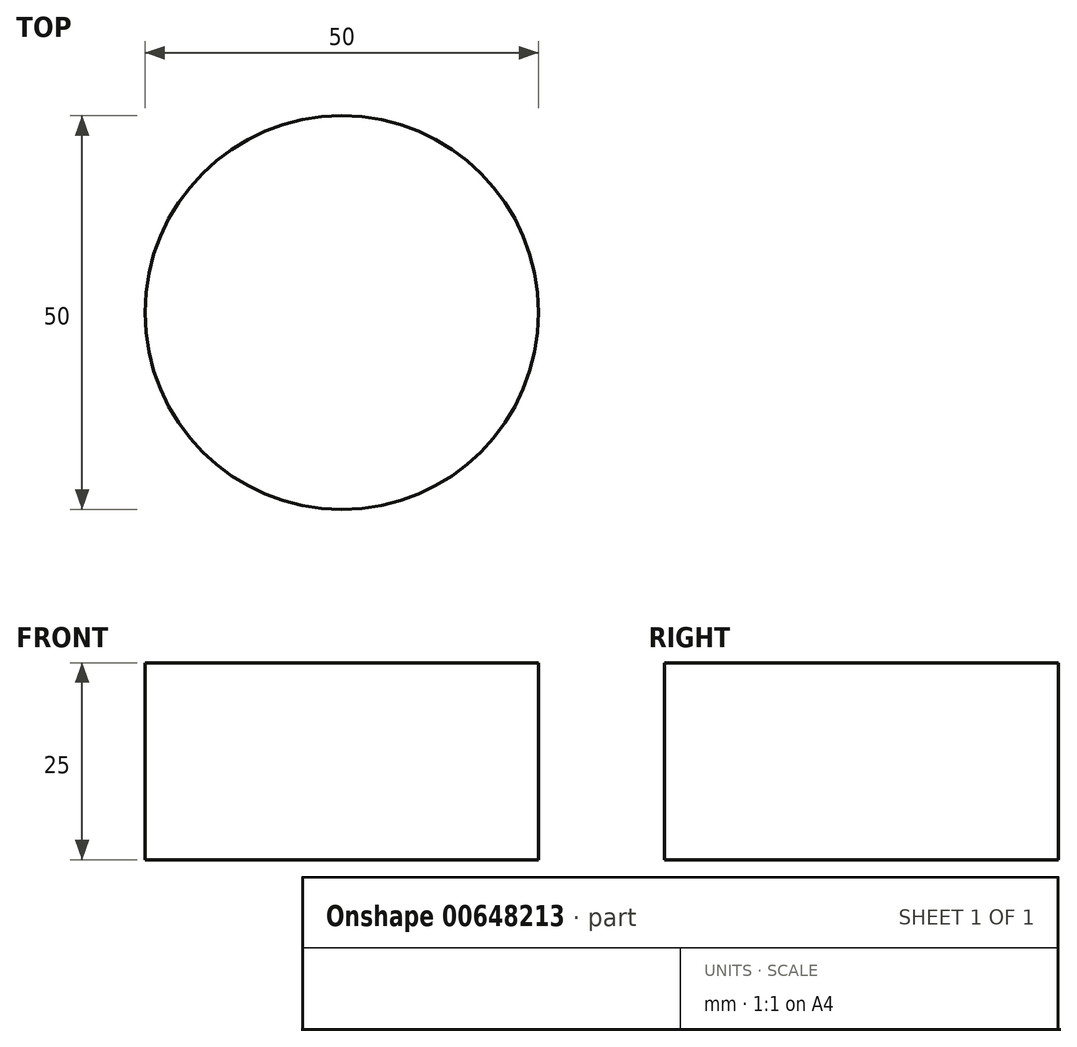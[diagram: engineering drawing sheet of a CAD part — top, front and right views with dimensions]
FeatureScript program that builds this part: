
annotation { "Feature Type Name" : "Feature", "Feature Type Description" : "" }
export const myFeature = defineFeature(function(context is Context, id is Id, definition is map)
    precondition{}
    {
        {
            var Q0;
            Q0=qCreatedBy(makeId("Top.planeOp"),FACE);
            var sketch = newSketch(context, id + "F0", { "sketchPlane" : qUnion([Q0])});
            skCircle(sketch, "E0", {"center": v(0, 0) * mm, "radius": 25 * mm});
            skSolve(sketch);
        }
        {
            var Q0;
            Q0=makeQuery(id+"F0.imprint","IMPRINT",FACE,{"disambiguationData":[TD([[makeQuery(id+"F0.imprint","IMPRINT",EDGE,{"derivedFrom":sQuery(id+"F0.wireOp",EDGE,"E0")}),1.0]])]});
            extrude(context, id + "F1", {"entities" : qUnion([Q0]), "depth" : 25 * mm, "offsetDistance" : 25 * mm});
        }
    });
